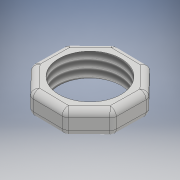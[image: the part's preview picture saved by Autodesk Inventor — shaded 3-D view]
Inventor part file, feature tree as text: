
AUTODESK INVENTOR PART (.ipt)
format: ipt  version: 2017 (Build 210142000, 142)  size: 158,720 bytes
history: native  units: mm
features: extrude x1, fillet x1, thread x1, sketch x1
ambient origin geometry x8: Origin, YZ Plane, XZ Plane, XY Plane, X Axis, Y Axis, Z Axis, Center Point
bodies: Solid1 (feature_tree)
feature tree (4):
  extrude  "Extrusion1"  Depth=6.0mm TaperAngle=0.0deg
  fillet  "Fillet1"  Radius=1.6mm
  thread  "Thread1"  [1 undecoded]
  sketch  "Sketch1"  dims[d0=16.0mm d1=6.0mm d2=0.0mm d3=1.6mm d4=10.0mm d5=0.0mm]
note: 1 required parameter value undecoded (feature->parameter linkage not recoverable at this tier; creation-order binding heuristic only, values carry confidence <= 0.55)
